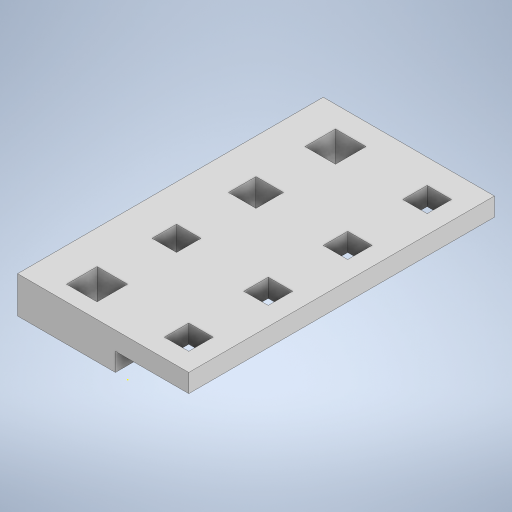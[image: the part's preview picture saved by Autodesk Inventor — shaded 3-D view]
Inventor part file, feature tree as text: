
AUTODESK INVENTOR PART (.ipt)
format: ipt  version: 2023 (Build 270158000, 158)  size: 290,304 bytes
history: native  units: mm
features: sketch x4, extrude x3
ambient origin geometry x8: Origin, YZ Plane, XZ Plane, XY Plane, X Axis, Y Axis, Z Axis, Center Point
bodies: Solid1 (feature_tree)
feature tree (7):
  extrude  "Extrusion1"  Depth=10.0mm
  extrude  "Extrusion2"  Depth=4.0mm
  extrude  "Extrusion3"  Depth=4.0mm
  sketch  "Sketch4"  dims[d6=4.0mm d7=9.0mm d8=4.0mm d9=9.0mm d10=4.0mm d11=9.0mm d12=4.0mm d13=2.0mm d14=3.0mm d15=0.0mm d16=6.0mm d17=16.0mm d18=0.0mm d19=5.0mm d20=5.0mm d21=5.0mm d22=5.0mm d23=4.0mm d24=4.0mm d25=4.5mm d26=4.5mm d27=16.0mm d28=0.0mm]
  sketch  "Sketch1"  dims[d0=50.0mm d1=10.0mm]
  sketch  "Sketch2"  dims[d2=90.0deg d3=4.0mm]
  sketch  "Sketch3"  dims[d4=2.0mm d5=4.0mm]
